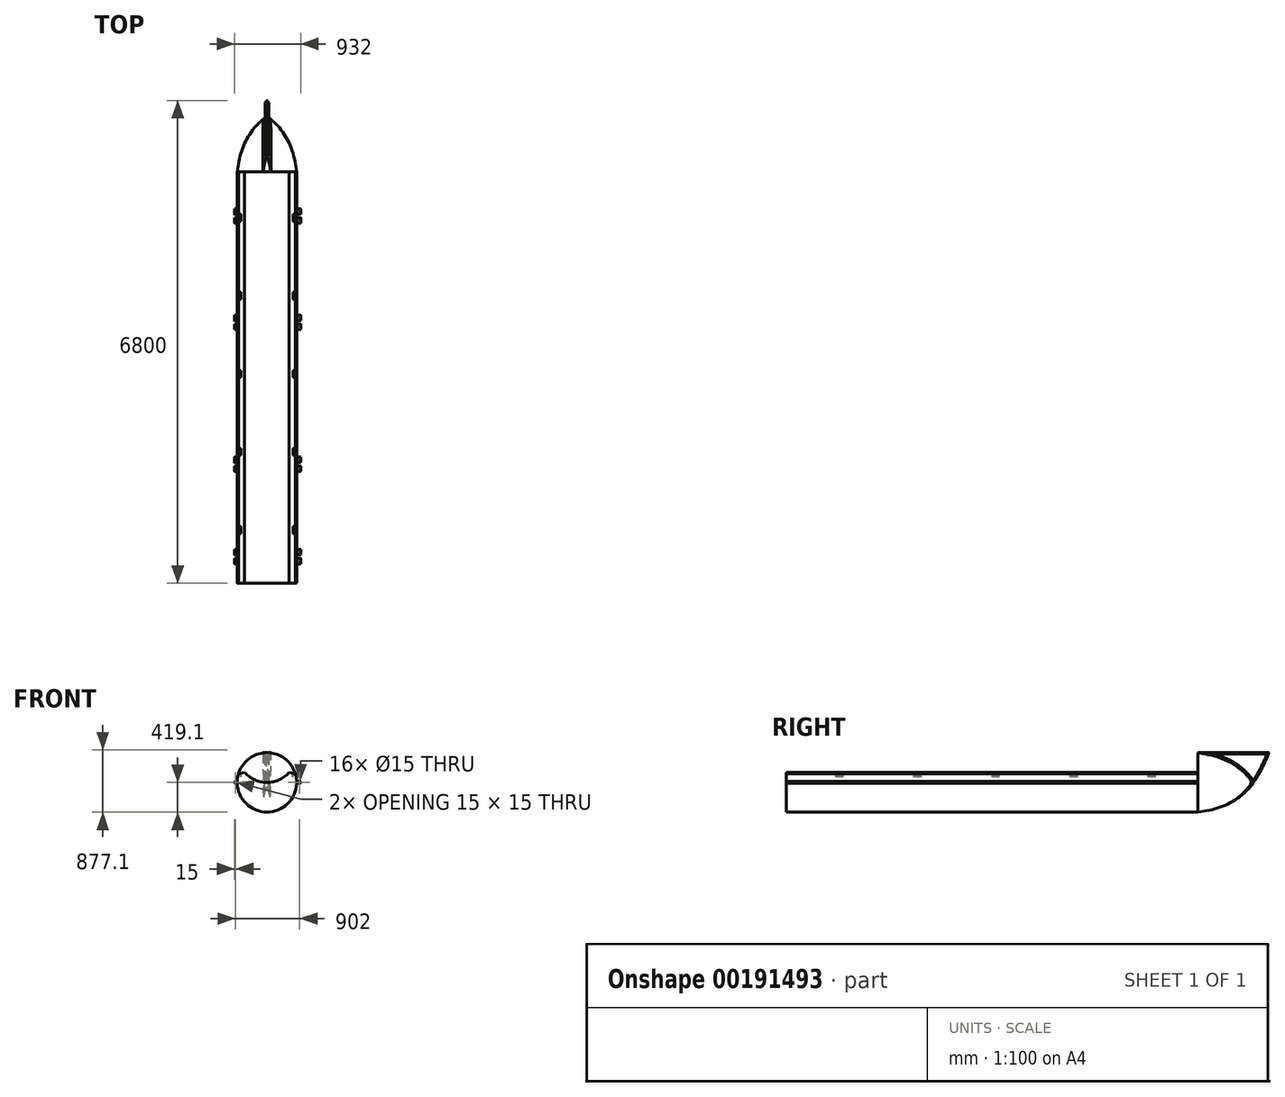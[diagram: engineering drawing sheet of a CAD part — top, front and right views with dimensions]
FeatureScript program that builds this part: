
annotation { "Feature Type Name" : "Feature", "Feature Type Description" : "" }
export const myFeature = defineFeature(function(context is Context, id is Id, definition is map)
    precondition{}
    {
        {
            var Q0;
            Q0=qCreatedBy(makeId("Front.planeOp"),FACE);
            var sketch = newSketch(context, id + "F0", { "sketchPlane" : qUnion([Q0])});
            skArc(sketch, "E0", {"start": v(-362.95, 209.55) * mm, "mid": v(0, -419.1) * mm, "end": v(362.95, 209.55) * mm});
            skArc(sketch, "E1", {"start": v(-362.95, 209.55) * mm, "mid": v(0, 0) * mm, "end": v(362.95, 209.55) * mm});
            skLineSegment(sketch, "E2", {"start": v(-364.87, 208.26) * mm, "end": v(699.86, 209.55) * mm, "construction": true});
            skLineSegment(sketch, "E3", {"start": v(0, -419.1) * mm, "end": v(871.37, -419.1) * mm, "construction": true});
            skSolve(sketch);
        }
        {
            var Q0;
            Q0=makeQuery(id+"F0.imprint","IMPRINT",FACE,{"disambiguationData":[TD([[makeQuery(id+"F0.imprint","IMPRINT",EDGE,{"derivedFrom":sQuery(id+"F0.wireOp",EDGE,"E0")}),1.0]])]});
            extrude(context, id + "F1", {"entities" : qUnion([Q0]), "depth" : 5800 * mm});
        }
        {
            var Q0;
            Q0=qCreatedBy(makeId("Right.planeOp"),FACE);
            var sketch = newSketch(context, id + "F2", { "sketchPlane" : qUnion([Q0])});
            skLineSegment(sketch, "E4", {"start": v(0, 419) * mm, "end": v(1000, 419) * mm});
            skLineSegment(sketch, "E5", {"start": v(0, 0) * mm, "end": v(0, 1274.52) * mm, "construction": true});
            skFitSpline(sketch, "E6", {"points": [v(1000, 419) * mm, v(0, -415.13) * mm], "startDerivative": vector(-568.6, -1416.71) * mm, "endDerivative": vector(-1840.67, -303.52) * mm});
            skLineSegment(sketch, "E7", {"start": v(0, 419) * mm, "end": v(0, -415.13) * mm});
            skSolve(sketch);
        }
        {
            var Q0;
            Q0 = qSketchRegion(id + "F2", true);
            extrude(context, id + "F3", {"entities" : qUnion([Q0]), "operationType" : NewBodyOperationType.ADD, "depth" : 25 * mm, "hasSecondDirection" : true, "secondDirectionOppositeDirection" : true, "secondDirectionDepth" : 25 * mm});
        }
        {
            var Q0;
            Q0=qCreatedBy(makeId("Right.planeOp"),FACE);
            var sketch = newSketch(context, id + "F4", { "sketchPlane" : qUnion([Q0])});
            skLineSegment(sketch, "E8", {"start": v(0, -0.1) * mm, "end": v(781.65, -0.1) * mm});
            skLineSegment(sketch, "E9", {"start": v(0, -0.1) * mm, "end": v(0, 1288.7) * mm, "construction": true});
            skFitSpline(sketch, "E10", {"points": [v(781.65, -0.1) * mm, v(0, -419.1) * mm], "startDerivative": vector(-633.97, -871.4) * mm, "endDerivative": vector(-828.07, -97.9) * mm});
            skLineSegment(sketch, "E11", {"start": v(0, -0.1) * mm, "end": v(0, -419.1) * mm});
            skLineSegment(sketch, "E12", {"start": v(0, -0.1) * mm, "end": v(1135.35, -0.1) * mm, "construction": true});
            skSolve(sketch);
        }
        {
            var Q0;
            Q0 = qSketchRegion(id + "F4", true);
            var Q1;
            Q1=sQuery(id+"F4.wireOp",EDGE,"E12");
            revolve(context, id + "F5", {"operationType" : NewBodyOperationType.ADD, "entities" : qUnion([Q0]), "axis" : qUnion([Q1]), "revolveType" : RevolveType.FULL});
        }
        {
            var Q0;
            Q0=makeQuery(id+"F5.boolean.opBoolean","INTERSECT",EDGE,{"derivedFrom":[makeQuery(id+"F3.opExtrude","CAP_FACE",FACE,{"disambiguationData":[OSD([sQuery(id+"F2.wireOp",EDGE,"E4"),sQuery(id+"F2.wireOp",EDGE,"E6"),sQuery(id+"F2.wireOp",EDGE,"E7")])],"isStart":true}),makeQuery(id+"F5.opRevolve","SWEPT_FACE",FACE,{"disambiguationData":[OSD([sQuery(id+"F4.wireOp",EDGE,"E10")])]})]});
            var Q1;
            Q1=makeQuery(id+"F5.boolean.opBoolean","INTERSECT",EDGE,{"derivedFrom":[makeQuery(id+"F3.opExtrude","CAP_FACE",FACE,{"disambiguationData":[OSD([sQuery(id+"F2.wireOp",EDGE,"E4"),sQuery(id+"F2.wireOp",EDGE,"E6"),sQuery(id+"F2.wireOp",EDGE,"E7")])],"isStart":false}),makeQuery(id+"F5.opRevolve","SWEPT_FACE",FACE,{"disambiguationData":[OSD([sQuery(id+"F4.wireOp",EDGE,"E10")])]})]});
            chamfer(context, id + "F6", {"entities" : qUnion([Q0, Q1]), "chamferType" : ChamferType.TWO_OFFSETS, "width1" : 35 * mm, "oppositeDirection" : false, "width2" : 25 * mm});
        }
        {
            var Q0;
            Q0=makeQuery(id+"F3.opExtrude","CAP_EDGE",EDGE,{"disambiguationData":[OSD([sQuery(id+"F2.wireOp",EDGE,"E4")])],"isStart":true});
            var Q1;
            Q1=makeQuery(id+"F3.opExtrude","CAP_EDGE",EDGE,{"disambiguationData":[OSD([sQuery(id+"F2.wireOp",EDGE,"E4")])],"isStart":false});
            var Q2;
            Q2=makeQuery(id+"F3.opExtrude","CAP_EDGE",EDGE,{"disambiguationData":[OSD([sQuery(id+"F2.wireOp",EDGE,"E6")])],"isStart":true});
            var Q3;
            Q3=makeQuery(id+"F3.opExtrude","CAP_EDGE",EDGE,{"disambiguationData":[OSD([sQuery(id+"F2.wireOp",EDGE,"E6")])],"isStart":false});
            var Q4;
            {var subQ0=sQuery(id+"F2.wireOp",EDGE,"E6");Q4=makeQuery(id+"F6.opChamfer","BLEND_EDGE",EDGE,{"blendedFrom":[makeQuery(id+"F5.boolean.opBoolean","INTERSECT",EDGE,{"derivedFrom":[makeQuery(id+"F3.opExtrude","CAP_FACE",FACE,{"disambiguationData":[OSD([sQuery(id+"F2.wireOp",EDGE,"E4"),subQ0,sQuery(id+"F2.wireOp",EDGE,"E7")])],"isStart":true}),makeQuery(id+"F5.opRevolve","SWEPT_FACE",FACE,{"disambiguationData":[OSD([sQuery(id+"F4.wireOp",EDGE,"E10")])]})]}),makeQuery(id+"F3.opExtrude","SWEPT_FACE",FACE,{"disambiguationData":[OSD([subQ0])]})],"blendedInto":[makeQuery(id+"F3.opExtrude","SWEPT_FACE",FACE,{"disambiguationData":[OSD([subQ0])]})]});}
            var Q5;
            {var subQ0=sQuery(id+"F2.wireOp",EDGE,"E6");Q5=makeQuery(id+"F6.opChamfer","BLEND_EDGE",EDGE,{"blendedFrom":[makeQuery(id+"F5.boolean.opBoolean","INTERSECT",EDGE,{"derivedFrom":[makeQuery(id+"F3.opExtrude","CAP_FACE",FACE,{"disambiguationData":[OSD([sQuery(id+"F2.wireOp",EDGE,"E4"),subQ0,sQuery(id+"F2.wireOp",EDGE,"E7")])],"isStart":false}),makeQuery(id+"F5.opRevolve","SWEPT_FACE",FACE,{"disambiguationData":[OSD([sQuery(id+"F4.wireOp",EDGE,"E10")])]})]}),makeQuery(id+"F3.opExtrude","SWEPT_FACE",FACE,{"disambiguationData":[OSD([subQ0])]})],"blendedInto":[makeQuery(id+"F3.opExtrude","SWEPT_FACE",FACE,{"disambiguationData":[OSD([subQ0])]})]});}
            chamfer(context, id + "F7", {"entities" : qUnion([Q0, Q1, Q2, Q3, Q4, Q5]), "width" : 20 * mm, "tangentPropagation" : true});
        }
        {
            var Q0;
            {var subQ0=sQuery(id+"F0.wireOp",EDGE,"E1");var subQ1=sQuery(id+"F0.wireOp",EDGE,"E0");Q0=makeQuery(id+"F1.opExtrude","SWEPT_EDGE",EDGE,{"disambiguationData":[OSD([subQ1,subQ0]),TDD([makeQuery(id+"F0.imprint","INTERSECT",VERTEX,{"disambiguationData":[OD(1.0)],"derivedFrom":[subQ1,subQ0]})])]});}
            var Q1;
            {var subQ0=sQuery(id+"F0.wireOp",EDGE,"E1");var subQ1=sQuery(id+"F0.wireOp",EDGE,"E0");Q1=makeQuery(id+"F1.opExtrude","SWEPT_EDGE",EDGE,{"disambiguationData":[OSD([subQ1,subQ0]),TDD([makeQuery(id+"F0.imprint","INTERSECT",VERTEX,{"disambiguationData":[OD(0.0)],"derivedFrom":[subQ1,subQ0]})])]});}
            chamfer(context, id + "F8", {"entities" : qUnion([Q0, Q1]), "width" : 50 * mm, "tangentPropagation" : true});
        }
        {
            var Q0;
            Q0=makeQuery(id+"F1.opExtrude","CAP_FACE",FACE,{"disambiguationData":[OSD([sQuery(id+"F0.wireOp",EDGE,"E0"),sQuery(id+"F0.wireOp",EDGE,"E1")])],"isStart":false});
            var sketch = newSketch(context, id + "F9", { "sketchPlane" : qUnion([Q0])});
            skLineSegment(sketch, "E13", {"start": v(0, 0) * mm, "end": v(315.98, 0) * mm, "construction": true});
            skLineSegment(sketch, "E14", {"start": v(0, 0) * mm, "end": v(0, 0) * mm});
            skLineSegment(sketch, "E15.bottom", {"start": v(0, -12.5) * mm, "end": v(475, -12.5) * mm});
            skLineSegment(sketch, "E15.top", {"start": v(0, 12.5) * mm, "end": v(475, 12.5) * mm});
            skLineSegment(sketch, "E15.left", {"start": v(0, -12.5) * mm, "end": v(0, 12.5) * mm});
            skLineSegment(sketch, "E15.right", {"start": v(475, -12.5) * mm, "end": v(475, 12.5) * mm});
            skLineSegment(sketch, "E16", {"start": v(-361.2, 166.04) * mm, "end": v(-241.62, -826.78) * mm, "construction": true});
            skLineSegment(sketch, "E17", {"start": v(432.02, 754.06) * mm, "end": v(312.43, -238.76) * mm, "construction": true});
            skLineSegment(sketch, "E18", {"start": v(-336.32, -40.51) * mm, "end": v(183.6, 22.11) * mm, "construction": true});
            skCircle(sketch, "E19", {"center": v(0.05, 419) * mm, "radius": 419 * mm});
            skPoint(sketch, "E20", {"position": v(0, 838) * mm});
            skLineSegment(sketch, "E21", {"start": v(-361.2, 166.04) * mm, "end": v(-361.2, 975.42) * mm, "construction": true});
            skCircle(sketch, "E22", {"center": v(460, 0) * mm, "radius": 7.5 * mm});
            skLineSegment(sketch, "E23.bottom", {"start": v(0, 12.5) * mm, "end": v(0, 12.5) * mm});
            skLineSegment(sketch, "E23.top", {"start": v(0, -12.5) * mm, "end": v(0, -12.5) * mm});
            skLineSegment(sketch, "E23.left", {"start": v(0, 12.5) * mm, "end": v(0, -12.5) * mm});
            skLineSegment(sketch, "E23.right", {"start": v(0, 12.5) * mm, "end": v(0, -12.5) * mm});
            skLineSegment(sketch, "E24.bottom", {"start": v(-457, -12.5) * mm, "end": v(0, -12.5) * mm});
            skLineSegment(sketch, "E24.top", {"start": v(-457, 12.5) * mm, "end": v(0, 12.5) * mm});
            skLineSegment(sketch, "E24.left", {"start": v(-457, -12.5) * mm, "end": v(-457, 12.5) * mm});
            skCircle(sketch, "E25", {"center": v(-442, 0) * mm, "radius": 7.5 * mm});
            skSolve(sketch);
        }
        {
            var Q0;
            {var subQ0=sQuery(id+"F9.wireOp",EDGE,"E15.right");Q0=makeQuery(id+"F9.imprint","IMPRINT",FACE,{"disambiguationData":[TD([[makeQuery(id+"F9.imprint","IMPRINT",EDGE,{"derivedFrom":subQ0}),1.0]])]});}
            var Q1;
            {var subQ0=sQuery(id+"F9.wireOp",EDGE,"E15.bottom");var subQ7=sQuery(id+"F9.wireOp",EDGE,"E15.left");var subQ8=makeQuery(id+"F9.imprint","INTERSECT",VERTEX,{"derivedFrom":[subQ0,subQ7]});Q1=makeQuery(id+"F9.imprint","IMPRINT",FACE,{"disambiguationData":[TD([[makeQuery(id+"F9.imprint","IMPRINT",EDGE,{"disambiguationData":[TD([[subQ8,-1.0]])],"derivedFrom":subQ0}),1.0]])]});}
            var Q2;
            {var subQ0=sQuery(id+"F9.wireOp",EDGE,"E24.left");Q2=makeQuery(id+"F9.imprint","IMPRINT",FACE,{"disambiguationData":[TD([[makeQuery(id+"F9.imprint","IMPRINT",EDGE,{"derivedFrom":subQ0}),-1.0]])]});}
            extrude(context, id + "F10", {"entities" : qUnion([Q0, Q1, Q2]), "operationType" : NewBodyOperationType.ADD, "oppositeDirection" : true, "depth" : 5800 * mm});
        }
        {
            var Q0;
            Q0=makeQuery(id+"F10.opExtrude","SWEPT_EDGE",EDGE,{"disambiguationData":[OSD([sQuery(id+"F9.wireOp",EDGE,"E15.bottom"),sQuery(id+"F9.wireOp",EDGE,"E15.right")])]});
            var Q1;
            Q1=makeQuery(id+"F10.opExtrude","SWEPT_EDGE",EDGE,{"disambiguationData":[OSD([sQuery(id+"F9.wireOp",EDGE,"E15.top"),sQuery(id+"F9.wireOp",EDGE,"E15.right")])]});
            var Q2;
            Q2=makeQuery(id+"F10.opExtrude","SWEPT_EDGE",EDGE,{"disambiguationData":[OSD([sQuery(id+"F9.wireOp",EDGE,"E24.top"),sQuery(id+"F9.wireOp",EDGE,"E24.left")])]});
            var Q3;
            Q3=makeQuery(id+"F10.opExtrude","SWEPT_EDGE",EDGE,{"disambiguationData":[OSD([sQuery(id+"F9.wireOp",EDGE,"E24.bottom"),sQuery(id+"F9.wireOp",EDGE,"E24.left")])]});
            fillet(context, id + "F11", {"entities" : qUnion([Q0, Q1, Q2, Q3]), "radius" : 12.5 * mm, "tangentPropagation" : true, "allowEdgeOverflow" : false});
        }
        {
            var Q0;
            {var subQ0=sQuery(id+"F0.wireOp",EDGE,"E1");var subQ1=sQuery(id+"F0.wireOp",EDGE,"E0");Q0=makeQuery(id+"F8.opChamfer","BLEND_FACE",FACE,{"disambiguationData":[OSD([subQ1,subQ0]),TDD([makeQuery(id+"F1.opExtrude","SWEPT_EDGE",EDGE,{"disambiguationData":[OSD([subQ1,subQ0]),TDD([makeQuery(id+"F0.imprint","INTERSECT",VERTEX,{"disambiguationData":[OD(0.0)],"derivedFrom":[subQ1,subQ0]})])]})])]});}
            var sketch = newSketch(context, id + "F12", { "sketchPlane" : qUnion([Q0])});
            skLineSegment(sketch, "E26.bottom", {"start": v(-343.82, -600) * mm, "end": v(-333.82, -600) * mm});
            skLineSegment(sketch, "E26.top", {"start": v(-343.82, -700) * mm, "end": v(-333.82, -700) * mm});
            skLineSegment(sketch, "E26.left", {"start": v(-343.82, -600) * mm, "end": v(-343.82, -700) * mm});
            skLineSegment(sketch, "E26.right", {"start": v(-333.82, -600) * mm, "end": v(-333.82, -700) * mm});
            skLineSegment(sketch, "E27.bottom", {"start": v(-343.82, -1700) * mm, "end": v(-333.82, -1700) * mm});
            skLineSegment(sketch, "E27.top", {"start": v(-343.82, -1800) * mm, "end": v(-333.82, -1800) * mm});
            skLineSegment(sketch, "E27.left", {"start": v(-343.82, -1700) * mm, "end": v(-343.82, -1800) * mm});
            skLineSegment(sketch, "E27.right", {"start": v(-333.82, -1700) * mm, "end": v(-333.82, -1800) * mm});
            skLineSegment(sketch, "E28.bottom", {"start": v(-343.7, -2800) * mm, "end": v(-333.7, -2800) * mm});
            skLineSegment(sketch, "E28.top", {"start": v(-343.7, -2900) * mm, "end": v(-333.7, -2900) * mm});
            skLineSegment(sketch, "E28.left", {"start": v(-343.7, -2800) * mm, "end": v(-343.7, -2900) * mm});
            skLineSegment(sketch, "E28.right", {"start": v(-333.7, -2800) * mm, "end": v(-333.7, -2900) * mm});
            skLineSegment(sketch, "E29.bottom", {"start": v(-333.7, -3900) * mm, "end": v(-343.7, -3900) * mm});
            skLineSegment(sketch, "E29.top", {"start": v(-333.7, -4000) * mm, "end": v(-343.7, -4000) * mm});
            skLineSegment(sketch, "E29.left", {"start": v(-333.7, -3900) * mm, "end": v(-333.7, -4000) * mm});
            skLineSegment(sketch, "E29.right", {"start": v(-343.7, -3900) * mm, "end": v(-343.7, -4000) * mm});
            skLineSegment(sketch, "E30.bottom", {"start": v(-343.7, -5000) * mm, "end": v(-333.7, -5000) * mm});
            skLineSegment(sketch, "E30.top", {"start": v(-343.7, -5100) * mm, "end": v(-333.7, -5100) * mm});
            skLineSegment(sketch, "E30.left", {"start": v(-343.7, -5000) * mm, "end": v(-343.7, -5100) * mm});
            skLineSegment(sketch, "E30.right", {"start": v(-333.7, -5000) * mm, "end": v(-333.7, -5100) * mm});
            skSolve(sketch);
        }
        {
            var Q0;
            Q0=makeQuery(id+"F12.imprint","IMPRINT",FACE,{"disambiguationData":[TD([[makeQuery(id+"F12.imprint","IMPRINT",EDGE,{"derivedFrom":sQuery(id+"F12.wireOp",EDGE,"E26.bottom")}),-1.0]])]});
            var Q1;
            Q1=makeQuery(id+"F12.imprint","IMPRINT",FACE,{"disambiguationData":[TD([[makeQuery(id+"F12.imprint","IMPRINT",EDGE,{"derivedFrom":sQuery(id+"F12.wireOp",EDGE,"E27.bottom")}),-1.0]])]});
            var Q2;
            Q2=makeQuery(id+"F12.imprint","IMPRINT",FACE,{"disambiguationData":[TD([[makeQuery(id+"F12.imprint","IMPRINT",EDGE,{"derivedFrom":sQuery(id+"F12.wireOp",EDGE,"E28.bottom")}),-1.0]])]});
            var Q3;
            Q3=makeQuery(id+"F12.imprint","IMPRINT",FACE,{"disambiguationData":[TD([[makeQuery(id+"F12.imprint","IMPRINT",EDGE,{"derivedFrom":sQuery(id+"F12.wireOp",EDGE,"E29.bottom")}),1.0]])]});
            var Q4;
            Q4=makeQuery(id+"F12.imprint","IMPRINT",FACE,{"disambiguationData":[TD([[makeQuery(id+"F12.imprint","IMPRINT",EDGE,{"derivedFrom":sQuery(id+"F12.wireOp",EDGE,"E30.bottom")}),-1.0]])]});
            extrude(context, id + "F13", {"entities" : qUnion([Q0, Q1, Q2, Q3, Q4]), "operationType" : NewBodyOperationType.REMOVE, "oppositeDirection" : true, "depth" : 50 * mm});
        }
        {
            var Q0;
            {var subQ0=sQuery(id+"F0.wireOp",EDGE,"E1");var subQ1=sQuery(id+"F0.wireOp",EDGE,"E0");Q0=makeQuery(id+"F8.opChamfer","BLEND_FACE",FACE,{"disambiguationData":[OSD([subQ1,subQ0]),TDD([makeQuery(id+"F1.opExtrude","SWEPT_EDGE",EDGE,{"disambiguationData":[OSD([subQ1,subQ0]),TDD([makeQuery(id+"F0.imprint","INTERSECT",VERTEX,{"disambiguationData":[OD(1.0)],"derivedFrom":[subQ1,subQ0]})])]})])]});}
            var sketch = newSketch(context, id + "F14", { "sketchPlane" : qUnion([Q0])});
            skLineSegment(sketch, "E31.bottom", {"start": v(333.82, -600) * mm, "end": v(343.82, -600) * mm});
            skLineSegment(sketch, "E31.top", {"start": v(333.82, -700) * mm, "end": v(343.82, -700) * mm});
            skLineSegment(sketch, "E31.left", {"start": v(333.82, -600) * mm, "end": v(333.82, -700) * mm});
            skLineSegment(sketch, "E31.right", {"start": v(343.82, -600) * mm, "end": v(343.82, -700) * mm});
            skLineSegment(sketch, "E32.bottom", {"start": v(333.82, -1700) * mm, "end": v(343.82, -1700) * mm});
            skLineSegment(sketch, "E32.top", {"start": v(333.82, -1800) * mm, "end": v(343.82, -1800) * mm});
            skLineSegment(sketch, "E32.left", {"start": v(333.82, -1700) * mm, "end": v(333.82, -1800) * mm});
            skLineSegment(sketch, "E32.right", {"start": v(343.82, -1700) * mm, "end": v(343.82, -1800) * mm});
            skLineSegment(sketch, "E33.bottom", {"start": v(333.7, -2800) * mm, "end": v(343.7, -2800) * mm});
            skLineSegment(sketch, "E33.top", {"start": v(333.7, -2900) * mm, "end": v(343.7, -2900) * mm});
            skLineSegment(sketch, "E33.left", {"start": v(333.7, -2800) * mm, "end": v(333.7, -2900) * mm});
            skLineSegment(sketch, "E33.right", {"start": v(343.7, -2800) * mm, "end": v(343.7, -2900) * mm});
            skLineSegment(sketch, "E34.bottom", {"start": v(343.7, -3900) * mm, "end": v(333.7, -3900) * mm});
            skLineSegment(sketch, "E34.top", {"start": v(343.7, -4000) * mm, "end": v(333.7, -4000) * mm});
            skLineSegment(sketch, "E34.left", {"start": v(343.7, -3900) * mm, "end": v(343.7, -4000) * mm});
            skLineSegment(sketch, "E34.right", {"start": v(333.7, -3900) * mm, "end": v(333.7, -4000) * mm});
            skLineSegment(sketch, "E35.bottom", {"start": v(333.7, -5000) * mm, "end": v(343.7, -5000) * mm});
            skLineSegment(sketch, "E35.top", {"start": v(333.7, -5100) * mm, "end": v(343.7, -5100) * mm});
            skLineSegment(sketch, "E35.left", {"start": v(333.7, -5000) * mm, "end": v(333.7, -5100) * mm});
            skLineSegment(sketch, "E35.right", {"start": v(343.7, -5000) * mm, "end": v(343.7, -5100) * mm});
            skSolve(sketch);
        }
        {
            var Q0;
            Q0=makeQuery(id+"F14.imprint","IMPRINT",FACE,{"disambiguationData":[TD([[makeQuery(id+"F14.imprint","IMPRINT",EDGE,{"derivedFrom":sQuery(id+"F14.wireOp",EDGE,"E32.bottom")}),-1.0]])]});
            var Q1;
            Q1=makeQuery(id+"F14.imprint","IMPRINT",FACE,{"disambiguationData":[TD([[makeQuery(id+"F14.imprint","IMPRINT",EDGE,{"derivedFrom":sQuery(id+"F14.wireOp",EDGE,"E31.bottom")}),-1.0]])]});
            var Q2;
            Q2=makeQuery(id+"F14.imprint","IMPRINT",FACE,{"disambiguationData":[TD([[makeQuery(id+"F14.imprint","IMPRINT",EDGE,{"derivedFrom":sQuery(id+"F14.wireOp",EDGE,"E33.bottom")}),-1.0]])]});
            var Q3;
            Q3=makeQuery(id+"F14.imprint","IMPRINT",FACE,{"disambiguationData":[TD([[makeQuery(id+"F14.imprint","IMPRINT",EDGE,{"derivedFrom":sQuery(id+"F14.wireOp",EDGE,"E34.bottom")}),1.0]])]});
            var Q4;
            Q4=makeQuery(id+"F14.imprint","IMPRINT",FACE,{"disambiguationData":[TD([[makeQuery(id+"F14.imprint","IMPRINT",EDGE,{"derivedFrom":sQuery(id+"F14.wireOp",EDGE,"E35.bottom")}),-1.0]])]});
            extrude(context, id + "F15", {"entities" : qUnion([Q0, Q1, Q2, Q3, Q4]), "operationType" : NewBodyOperationType.REMOVE, "oppositeDirection" : true, "depth" : 50 * mm});
        }
        {
            var Q0;
            Q0=makeQuery(id+"F10.opExtrude","SWEPT_FACE",FACE,{"disambiguationData":[OSD([sQuery(id+"F9.wireOp",EDGE,"E15.top")])]});
            var sketch = newSketch(context, id + "F16", { "sketchPlane" : qUnion([Q0])});
            skLineSegment(sketch, "E36.bottom", {"start": v(418.91, 0) * mm, "end": v(478.91, 0) * mm});
            skLineSegment(sketch, "E36.top", {"start": v(418.91, -525) * mm, "end": v(478.91, -525) * mm});
            skLineSegment(sketch, "E36.left", {"start": v(418.91, 0) * mm, "end": v(418.91, -525) * mm});
            skLineSegment(sketch, "E36.right", {"start": v(478.91, 0) * mm, "end": v(478.91, -525) * mm});
            skLineSegment(sketch, "E37.bottom", {"start": v(418.91, -600) * mm, "end": v(478.91, -600) * mm});
            skLineSegment(sketch, "E37.top", {"start": v(418.91, -650) * mm, "end": v(478.91, -650) * mm});
            skLineSegment(sketch, "E37.left", {"start": v(418.91, -600) * mm, "end": v(418.91, -650) * mm});
            skLineSegment(sketch, "E37.right", {"start": v(478.91, -600) * mm, "end": v(478.91, -650) * mm});
            skLineSegment(sketch, "E38.bottom", {"start": v(418.91, -725) * mm, "end": v(478.91, -725) * mm});
            skLineSegment(sketch, "E38.top", {"start": v(418.91, -2025) * mm, "end": v(478.91, -2025) * mm});
            skLineSegment(sketch, "E38.left", {"start": v(418.91, -725) * mm, "end": v(418.91, -2025) * mm});
            skLineSegment(sketch, "E38.right", {"start": v(478.91, -725) * mm, "end": v(478.91, -2025) * mm});
            skLineSegment(sketch, "E39", {"start": v(321.16, -625) * mm, "end": v(900.18, -625) * mm, "construction": true});
            skPoint(sketch, "E39.endSnap0", {"position": v(418.91, -625) * mm});
            skLineSegment(sketch, "E40.bottom", {"start": v(418.91, -2100) * mm, "end": v(478.91, -2100) * mm});
            skLineSegment(sketch, "E40.top", {"start": v(418.91, -2150) * mm, "end": v(478.91, -2150) * mm});
            skLineSegment(sketch, "E40.left", {"start": v(418.91, -2100) * mm, "end": v(418.91, -2150) * mm});
            skLineSegment(sketch, "E40.right", {"start": v(478.91, -2100) * mm, "end": v(478.91, -2150) * mm});
            skLineSegment(sketch, "E41", {"start": v(301.17, -2125) * mm, "end": v(700.35, -2125) * mm, "construction": true});
            skLineSegment(sketch, "E42.top", {"start": v(418.91, 0) * mm, "end": v(473.91, 0) * mm});
            skLineSegment(sketch, "E43.bottom", {"start": v(418.91, -4100) * mm, "end": v(478.91, -4100) * mm});
            skLineSegment(sketch, "E43.top", {"start": v(418.91, -4150) * mm, "end": v(478.91, -4150) * mm});
            skLineSegment(sketch, "E43.left", {"start": v(418.91, -4100) * mm, "end": v(418.91, -4150) * mm});
            skLineSegment(sketch, "E43.right", {"start": v(478.91, -4100) * mm, "end": v(478.91, -4150) * mm});
            skLineSegment(sketch, "E44", {"start": v(343.46, -4125) * mm, "end": v(552.93, -4125) * mm, "construction": true});
            skPoint(sketch, "E44.startSnap0", {"position": v(418.91, -4125) * mm});
            skPoint(sketch, "E44.endSnap0", {"position": v(418.91, -4125) * mm});
            skLineSegment(sketch, "E45.bottom", {"start": v(418.91, -5400) * mm, "end": v(478.91, -5400) * mm});
            skLineSegment(sketch, "E45.top", {"start": v(418.91, -5450) * mm, "end": v(478.91, -5450) * mm});
            skLineSegment(sketch, "E45.left", {"start": v(418.91, -5400) * mm, "end": v(418.91, -5450) * mm});
            skLineSegment(sketch, "E45.right", {"start": v(478.91, -5400) * mm, "end": v(478.91, -5450) * mm});
            skLineSegment(sketch, "E46", {"start": v(317, -5425) * mm, "end": v(574.63, -5425) * mm, "construction": true});
            skLineSegment(sketch, "E47.bottom", {"start": v(478.91, -4025) * mm, "end": v(418.91, -4025) * mm});
            skLineSegment(sketch, "E47.top", {"start": v(478.91, -2225) * mm, "end": v(418.91, -2225) * mm});
            skLineSegment(sketch, "E47.left", {"start": v(478.91, -4025) * mm, "end": v(478.91, -2225) * mm});
            skLineSegment(sketch, "E47.right", {"start": v(418.91, -4025) * mm, "end": v(418.91, -2225) * mm});
            skLineSegment(sketch, "E48.bottom", {"start": v(418.91, -4225) * mm, "end": v(478.91, -4225) * mm});
            skLineSegment(sketch, "E48.top", {"start": v(418.91, -5325) * mm, "end": v(478.91, -5325) * mm});
            skLineSegment(sketch, "E48.left", {"start": v(418.91, -4225) * mm, "end": v(418.91, -5325) * mm});
            skLineSegment(sketch, "E48.right", {"start": v(478.91, -4225) * mm, "end": v(478.91, -5325) * mm});
            skLineSegment(sketch, "E49.bottom", {"start": v(418.91, -5525) * mm, "end": v(478.91, -5525) * mm});
            skLineSegment(sketch, "E49.top", {"start": v(418.91, -5800) * mm, "end": v(478.91, -5800) * mm});
            skLineSegment(sketch, "E49.left", {"start": v(418.91, -5525) * mm, "end": v(418.91, -5800) * mm});
            skLineSegment(sketch, "E49.right", {"start": v(478.91, -5525) * mm, "end": v(478.91, -5800) * mm});
            skLineSegment(sketch, "E50", {"start": v(0, 0) * mm, "end": v(0, -6000) * mm, "construction": true});
            skLineSegment(sketch, "E51.bottom", {"start": v(-473.91, 0) * mm, "end": v(-418.91, 0) * mm});
            skLineSegment(sketch, "E51.top", {"start": v(-473.91, -525) * mm, "end": v(-418.91, -525) * mm});
            skLineSegment(sketch, "E51.left", {"start": v(-473.91, 0) * mm, "end": v(-473.91, -525) * mm});
            skLineSegment(sketch, "E51.right", {"start": v(-418.91, 0) * mm, "end": v(-418.91, -525) * mm});
            skLineSegment(sketch, "E52.bottom", {"start": v(-473.91, -600) * mm, "end": v(-418.91, -600) * mm});
            skLineSegment(sketch, "E52.top", {"start": v(-473.91, -650) * mm, "end": v(-418.91, -650) * mm});
            skLineSegment(sketch, "E52.left", {"start": v(-473.91, -600) * mm, "end": v(-473.91, -650) * mm});
            skLineSegment(sketch, "E52.right", {"start": v(-418.91, -600) * mm, "end": v(-418.91, -650) * mm});
            skLineSegment(sketch, "E53.bottom", {"start": v(-473.91, -725) * mm, "end": v(-418.91, -725) * mm});
            skLineSegment(sketch, "E53.top", {"start": v(-473.91, -2025) * mm, "end": v(-418.91, -2025) * mm});
            skLineSegment(sketch, "E53.left", {"start": v(-473.91, -725) * mm, "end": v(-473.91, -2025) * mm});
            skLineSegment(sketch, "E53.right", {"start": v(-418.91, -725) * mm, "end": v(-418.91, -2025) * mm});
            skLineSegment(sketch, "E54", {"start": v(-855.24, -625) * mm, "end": v(-276.22, -625) * mm, "construction": true});
            skPoint(sketch, "E54.endSnap0", {"position": v(-473.91, -625) * mm});
            skLineSegment(sketch, "E55.bottom", {"start": v(-473.91, -2100) * mm, "end": v(-418.91, -2100) * mm});
            skLineSegment(sketch, "E55.top", {"start": v(-473.91, -2150) * mm, "end": v(-418.91, -2150) * mm});
            skLineSegment(sketch, "E55.left", {"start": v(-473.91, -2100) * mm, "end": v(-473.91, -2150) * mm});
            skLineSegment(sketch, "E55.right", {"start": v(-418.91, -2100) * mm, "end": v(-418.91, -2150) * mm});
            skLineSegment(sketch, "E56", {"start": v(-875.23, -2125) * mm, "end": v(-476.05, -2125) * mm, "construction": true});
            skLineSegment(sketch, "E57.top", {"start": v(-757.49, 1788.3) * mm, "end": v(-702.49, 1788.3) * mm});
            skLineSegment(sketch, "E58.bottom", {"start": v(-473.91, -4100) * mm, "end": v(-418.91, -4100) * mm});
            skLineSegment(sketch, "E58.top", {"start": v(-473.91, -4150) * mm, "end": v(-418.91, -4150) * mm});
            skLineSegment(sketch, "E58.left", {"start": v(-473.91, -4100) * mm, "end": v(-473.91, -4150) * mm});
            skLineSegment(sketch, "E58.right", {"start": v(-418.91, -4100) * mm, "end": v(-418.91, -4150) * mm});
            skLineSegment(sketch, "E59", {"start": v(-832.94, -4125) * mm, "end": v(-623.47, -4125) * mm, "construction": true});
            skPoint(sketch, "E59.startSnap0", {"position": v(-473.91, -4125) * mm});
            skPoint(sketch, "E59.endSnap0", {"position": v(-473.91, -4125) * mm});
            skLineSegment(sketch, "E60.bottom", {"start": v(-473.91, -5400) * mm, "end": v(-418.91, -5400) * mm});
            skLineSegment(sketch, "E60.top", {"start": v(-473.91, -5450) * mm, "end": v(-418.91, -5450) * mm});
            skLineSegment(sketch, "E60.left", {"start": v(-473.91, -5400) * mm, "end": v(-473.91, -5450) * mm});
            skLineSegment(sketch, "E60.right", {"start": v(-418.91, -5400) * mm, "end": v(-418.91, -5450) * mm});
            skLineSegment(sketch, "E61", {"start": v(-859.4, -5425) * mm, "end": v(-601.77, -5425) * mm, "construction": true});
            skLineSegment(sketch, "E62.bottom", {"start": v(-418.91, -4025) * mm, "end": v(-473.91, -4025) * mm});
            skLineSegment(sketch, "E62.top", {"start": v(-418.91, -2225) * mm, "end": v(-473.91, -2225) * mm});
            skLineSegment(sketch, "E62.left", {"start": v(-418.91, -4025) * mm, "end": v(-418.91, -2225) * mm});
            skLineSegment(sketch, "E62.right", {"start": v(-473.91, -4025) * mm, "end": v(-473.91, -2225) * mm});
            skLineSegment(sketch, "E63.bottom", {"start": v(-473.91, -4225) * mm, "end": v(-418.91, -4225) * mm});
            skLineSegment(sketch, "E63.top", {"start": v(-473.91, -5325) * mm, "end": v(-418.91, -5325) * mm});
            skLineSegment(sketch, "E63.left", {"start": v(-473.91, -4225) * mm, "end": v(-473.91, -5325) * mm});
            skLineSegment(sketch, "E63.right", {"start": v(-418.91, -4225) * mm, "end": v(-418.91, -5325) * mm});
            skLineSegment(sketch, "E64.bottom", {"start": v(-473.91, -5525) * mm, "end": v(-418.91, -5525) * mm});
            skLineSegment(sketch, "E64.top", {"start": v(-473.91, -5800) * mm, "end": v(-418.91, -5800) * mm});
            skLineSegment(sketch, "E64.left", {"start": v(-473.91, -5525) * mm, "end": v(-473.91, -5800) * mm});
            skLineSegment(sketch, "E64.right", {"start": v(-418.91, -5525) * mm, "end": v(-418.91, -5800) * mm});
            skLineSegment(sketch, "E65", {"start": v(-1176.4, 1788.3) * mm, "end": v(-1176.4, -4211.7) * mm, "construction": true});
            skSolve(sketch);
        }
        {
            var Q0;
            {var subQ0=sQuery(id+"F16.wireOp",EDGE,"E36.left");Q0=makeQuery(id+"F16.imprint","IMPRINT",FACE,{"disambiguationData":[TD([[makeQuery(id+"F16.imprint","IMPRINT",EDGE,{"derivedFrom":subQ0}),1.0]])]});}
            var Q1;
            {var subQ0=sQuery(id+"F16.wireOp",EDGE,"E36.right");Q1=makeQuery(id+"F16.imprint","IMPRINT",FACE,{"disambiguationData":[TD([[makeQuery(id+"F16.imprint","IMPRINT",EDGE,{"derivedFrom":subQ0}),-1.0]])]});}
            var Q2;
            {var subQ0=sQuery(id+"F16.wireOp",EDGE,"E37.left");Q2=makeQuery(id+"F16.imprint","IMPRINT",FACE,{"disambiguationData":[TD([[makeQuery(id+"F16.imprint","IMPRINT",EDGE,{"derivedFrom":subQ0}),1.0]])]});}
            var Q3;
            {var subQ0=sQuery(id+"F16.wireOp",EDGE,"E37.right");Q3=makeQuery(id+"F16.imprint","IMPRINT",FACE,{"disambiguationData":[TD([[makeQuery(id+"F16.imprint","IMPRINT",EDGE,{"derivedFrom":subQ0}),-1.0]])]});}
            var Q4;
            {var subQ0=sQuery(id+"F16.wireOp",EDGE,"E38.left");Q4=makeQuery(id+"F16.imprint","IMPRINT",FACE,{"disambiguationData":[TD([[makeQuery(id+"F16.imprint","IMPRINT",EDGE,{"derivedFrom":subQ0}),1.0]])]});}
            var Q5;
            {var subQ0=sQuery(id+"F16.wireOp",EDGE,"E38.right");Q5=makeQuery(id+"F16.imprint","IMPRINT",FACE,{"disambiguationData":[TD([[makeQuery(id+"F16.imprint","IMPRINT",EDGE,{"derivedFrom":subQ0}),-1.0]])]});}
            var Q6;
            {var subQ0=sQuery(id+"F16.wireOp",EDGE,"E40.left");Q6=makeQuery(id+"F16.imprint","IMPRINT",FACE,{"disambiguationData":[TD([[makeQuery(id+"F16.imprint","IMPRINT",EDGE,{"derivedFrom":subQ0}),1.0]])]});}
            var Q7;
            {var subQ0=sQuery(id+"F16.wireOp",EDGE,"E40.right");Q7=makeQuery(id+"F16.imprint","IMPRINT",FACE,{"disambiguationData":[TD([[makeQuery(id+"F16.imprint","IMPRINT",EDGE,{"derivedFrom":subQ0}),-1.0]])]});}
            var Q8;
            {var subQ0=sQuery(id+"F16.wireOp",EDGE,"E47.left");Q8=makeQuery(id+"F16.imprint","IMPRINT",FACE,{"disambiguationData":[TD([[makeQuery(id+"F16.imprint","IMPRINT",EDGE,{"derivedFrom":subQ0}),1.0]])]});}
            var Q9;
            {var subQ0=sQuery(id+"F16.wireOp",EDGE,"E47.right");Q9=makeQuery(id+"F16.imprint","IMPRINT",FACE,{"disambiguationData":[TD([[makeQuery(id+"F16.imprint","IMPRINT",EDGE,{"derivedFrom":subQ0}),1.0]])]});}
            var Q10;
            {var subQ0=sQuery(id+"F16.wireOp",EDGE,"E43.left");Q10=makeQuery(id+"F16.imprint","IMPRINT",FACE,{"disambiguationData":[TD([[makeQuery(id+"F16.imprint","IMPRINT",EDGE,{"derivedFrom":subQ0}),1.0]])]});}
            var Q11;
            {var subQ0=sQuery(id+"F16.wireOp",EDGE,"E43.right");Q11=makeQuery(id+"F16.imprint","IMPRINT",FACE,{"disambiguationData":[TD([[makeQuery(id+"F16.imprint","IMPRINT",EDGE,{"derivedFrom":subQ0}),-1.0]])]});}
            var Q12;
            {var subQ0=sQuery(id+"F16.wireOp",EDGE,"E48.left");Q12=makeQuery(id+"F16.imprint","IMPRINT",FACE,{"disambiguationData":[TD([[makeQuery(id+"F16.imprint","IMPRINT",EDGE,{"derivedFrom":subQ0}),1.0]])]});}
            var Q13;
            {var subQ0=sQuery(id+"F16.wireOp",EDGE,"E48.right");Q13=makeQuery(id+"F16.imprint","IMPRINT",FACE,{"disambiguationData":[TD([[makeQuery(id+"F16.imprint","IMPRINT",EDGE,{"derivedFrom":subQ0}),-1.0]])]});}
            var Q14;
            {var subQ0=sQuery(id+"F16.wireOp",EDGE,"E49.left");Q14=makeQuery(id+"F16.imprint","IMPRINT",FACE,{"disambiguationData":[TD([[makeQuery(id+"F16.imprint","IMPRINT",EDGE,{"derivedFrom":subQ0}),1.0]])]});}
            var Q15;
            {var subQ0=sQuery(id+"F16.wireOp",EDGE,"E49.right");Q15=makeQuery(id+"F16.imprint","IMPRINT",FACE,{"disambiguationData":[TD([[makeQuery(id+"F16.imprint","IMPRINT",EDGE,{"derivedFrom":subQ0}),-1.0]])]});}
            var Q16;
            {var subQ0=sQuery(id+"F16.wireOp",EDGE,"E45.left");Q16=makeQuery(id+"F16.imprint","IMPRINT",FACE,{"disambiguationData":[TD([[makeQuery(id+"F16.imprint","IMPRINT",EDGE,{"derivedFrom":subQ0}),1.0]])]});}
            var Q17;
            {var subQ0=sQuery(id+"F16.wireOp",EDGE,"E45.right");Q17=makeQuery(id+"F16.imprint","IMPRINT",FACE,{"disambiguationData":[TD([[makeQuery(id+"F16.imprint","IMPRINT",EDGE,{"derivedFrom":subQ0}),-1.0]])]});}
            var Q18;
            Q18=makeQuery(id+"F16.imprint","IMPRINT",FACE,{"disambiguationData":[TD([[makeQuery(id+"F16.imprint","IMPRINT",EDGE,{"derivedFrom":sQuery(id+"F16.wireOp",EDGE,"E51.bottom")}),-1.0]])]});
            var Q19;
            Q19=makeQuery(id+"F16.imprint","IMPRINT",FACE,{"disambiguationData":[TD([[makeQuery(id+"F16.imprint","IMPRINT",EDGE,{"derivedFrom":sQuery(id+"F16.wireOp",EDGE,"E52.bottom")}),-1.0]])]});
            var Q20;
            Q20=makeQuery(id+"F16.imprint","IMPRINT",FACE,{"disambiguationData":[TD([[makeQuery(id+"F16.imprint","IMPRINT",EDGE,{"derivedFrom":sQuery(id+"F16.wireOp",EDGE,"E62.bottom")}),-1.0]])]});
            var Q21;
            Q21=makeQuery(id+"F16.imprint","IMPRINT",FACE,{"disambiguationData":[TD([[makeQuery(id+"F16.imprint","IMPRINT",EDGE,{"derivedFrom":sQuery(id+"F16.wireOp",EDGE,"E55.bottom")}),-1.0]])]});
            var Q22;
            Q22=makeQuery(id+"F16.imprint","IMPRINT",FACE,{"disambiguationData":[TD([[makeQuery(id+"F16.imprint","IMPRINT",EDGE,{"derivedFrom":sQuery(id+"F16.wireOp",EDGE,"E53.bottom")}),-1.0]])]});
            var Q23;
            Q23=makeQuery(id+"F16.imprint","IMPRINT",FACE,{"disambiguationData":[TD([[makeQuery(id+"F16.imprint","IMPRINT",EDGE,{"derivedFrom":sQuery(id+"F16.wireOp",EDGE,"E64.bottom")}),-1.0]])]});
            var Q24;
            Q24=makeQuery(id+"F16.imprint","IMPRINT",FACE,{"disambiguationData":[TD([[makeQuery(id+"F16.imprint","IMPRINT",EDGE,{"derivedFrom":sQuery(id+"F16.wireOp",EDGE,"E60.bottom")}),-1.0]])]});
            var Q25;
            Q25=makeQuery(id+"F16.imprint","IMPRINT",FACE,{"disambiguationData":[TD([[makeQuery(id+"F16.imprint","IMPRINT",EDGE,{"derivedFrom":sQuery(id+"F16.wireOp",EDGE,"E63.bottom")}),-1.0]])]});
            var Q26;
            Q26=makeQuery(id+"F16.imprint","IMPRINT",FACE,{"disambiguationData":[TD([[makeQuery(id+"F16.imprint","IMPRINT",EDGE,{"derivedFrom":sQuery(id+"F16.wireOp",EDGE,"E58.bottom")}),-1.0]])]});
            extrude(context, id + "F17", {"entities" : qUnion([Q0, Q1, Q2, Q3, Q4, Q5, Q6, Q7, Q8, Q9, Q10, Q11, Q12, Q13, Q14, Q15, Q16, Q17, Q18, Q19, Q20, Q21, Q22, Q23, Q24, Q25, Q26]), "operationType" : NewBodyOperationType.REMOVE, "oppositeDirection" : true, "depth" : 50 * mm, "hasSecondDirection" : true, "secondDirectionOppositeDirection" : false, "secondDirectionDepth" : 50 * mm});
        }
    });
